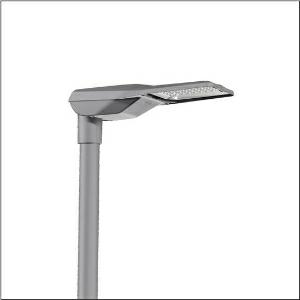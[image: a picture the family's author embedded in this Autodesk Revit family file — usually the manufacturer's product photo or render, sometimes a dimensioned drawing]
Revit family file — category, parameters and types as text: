
# Revit family: streetlight_sl_21_iq_mini___p0_8ab_5xe2r31d08gb_0de2
name_source: partatom
category: Lighting Fixtures
units: mm (PartAtom-declared; Revit-internal decimal feet)

## family parameters
Cut with Voids When Loaded = No
Host = Face
Light Source = No
Part Type = Normal
Room Calculation Point = No
Round Connector Dimension = Use Diameter
Shared = No

## types (1)
- --- (1 x LED, 4930 lm, 37.1 W, 3000K)
    Apparent Load = 37 VA
    CIE Flux Codes = 36 71 98 100 100
    Color Rendering = 70
    Color Temperature = 3000K
    Default Elevation = 1800 mm
    Description = Streetlight SL 21 iQ mini, mast luminaire, primary light control with lens, of PMMA, primary optical cover: cover, of toughened safety glass, transparent, light distribution: P0.8aB, light emission: direct distribution, primary light characteristic: asymmetric, installation type: post-top, side-entry, LED, High Power LED, rated luminous flux: 4.930lm, luminous efficacy: 133lm/W, light colour: 730, colour temperature: 3000K, control gear: iQ-Comfort, control: pre-setting: linear dimming characteristic, Auto-Match, Temp-Guard, Lumen-Switch, Night-Set, Smart-Wire, Light-Fading, Desk-Remote (wireless, voltage-free reading and setting of iQ features in the workshop via application-optimized NFC function/RFID function), optimised constant luminous flux control (CLO 2.0), mains connection: 220..240V, AC, 50/60Hz, start of lifetime: 37W, end of service life: 39W, reduction: 18W, luminaire housing, of diecast aluminium, powder-coated, Siteco® metallic grey (DB 702S), corrosivity category C5 mid according to DIN EN ISO 12944, please order mast flange separately, inclination adjustable: 0°, 5°, 10°, 15°, sealing non-destructively replaceable, multi-level sealing system, length: 628mm, width: 235mm, height: 110mm, mast flange for spigot size: 42mm (side-entry): 5XC10008XM4, 60/48mm (side-entry/post-top): 5XC10108XM2, 76/60mm (side-entry/post-top): 5XC10108XM1, mounting height: 4..8m, protection rating (complete): IP66, insulation class (complete): insulation class II (safety insulation), certification: CE, ENEC, ENEC+, VDE, impact resistance: IK10, permissible operating ambient temperature for outdoor applications: -40..+50°C, standard-compliant lighting for roads and squares, packaging unit: 1 piece

Light Distribution: P0.8aB
    Height = 110 mm
    Lamp = 1 x LED
    Lamp Light Flux = 4930 lm
    Lamp Power = 37.1 W
    Lamp count = 1
    Length = 625 mm
    Luminous efficacy = 133 lm/W
    Manufacturer = Siteco
    ModVariant = No
    Model = 5XE2R31D08GB
    Number of Poles = 1
    OnlyDefault = Yes
    Power Factor = 1
    Product Name = Streetlight SL 21 iQ mini | P0.8aB
    Product group = mast luminaire | pylon top
    ProductGroupID = 6100
    Protection Class = Protection class II
    Protection Degree = IP 66
    RLX_Detail_Level = 1
    RLX_Emergency_Light_Flux = 0 lm
    RLX_Emergency_Type = 0
    RLX_Emergency_Type_DB = No
    RlxData = <blob elided: 26005 chars, md5=8ad6de04>
    Socket = socket
    Standby Power = 0 W
    System Light Flux = 4930 lm
    System Power = 37 W
    Type Comments = factory setting: luminous flux: 100 % | dim-lin: 254 | 385 mA
    Type Image = l_1003519.jpg
    URL = http://relux.com
    VarID = @adj_074560
    Voltage = 0 V
    Weight = 0.00 kg
    Width = 234 mm

## geometry (parser evidence)
native form markers: Blend x4, Sweep x11
no freeform markers — native parametric forms only
